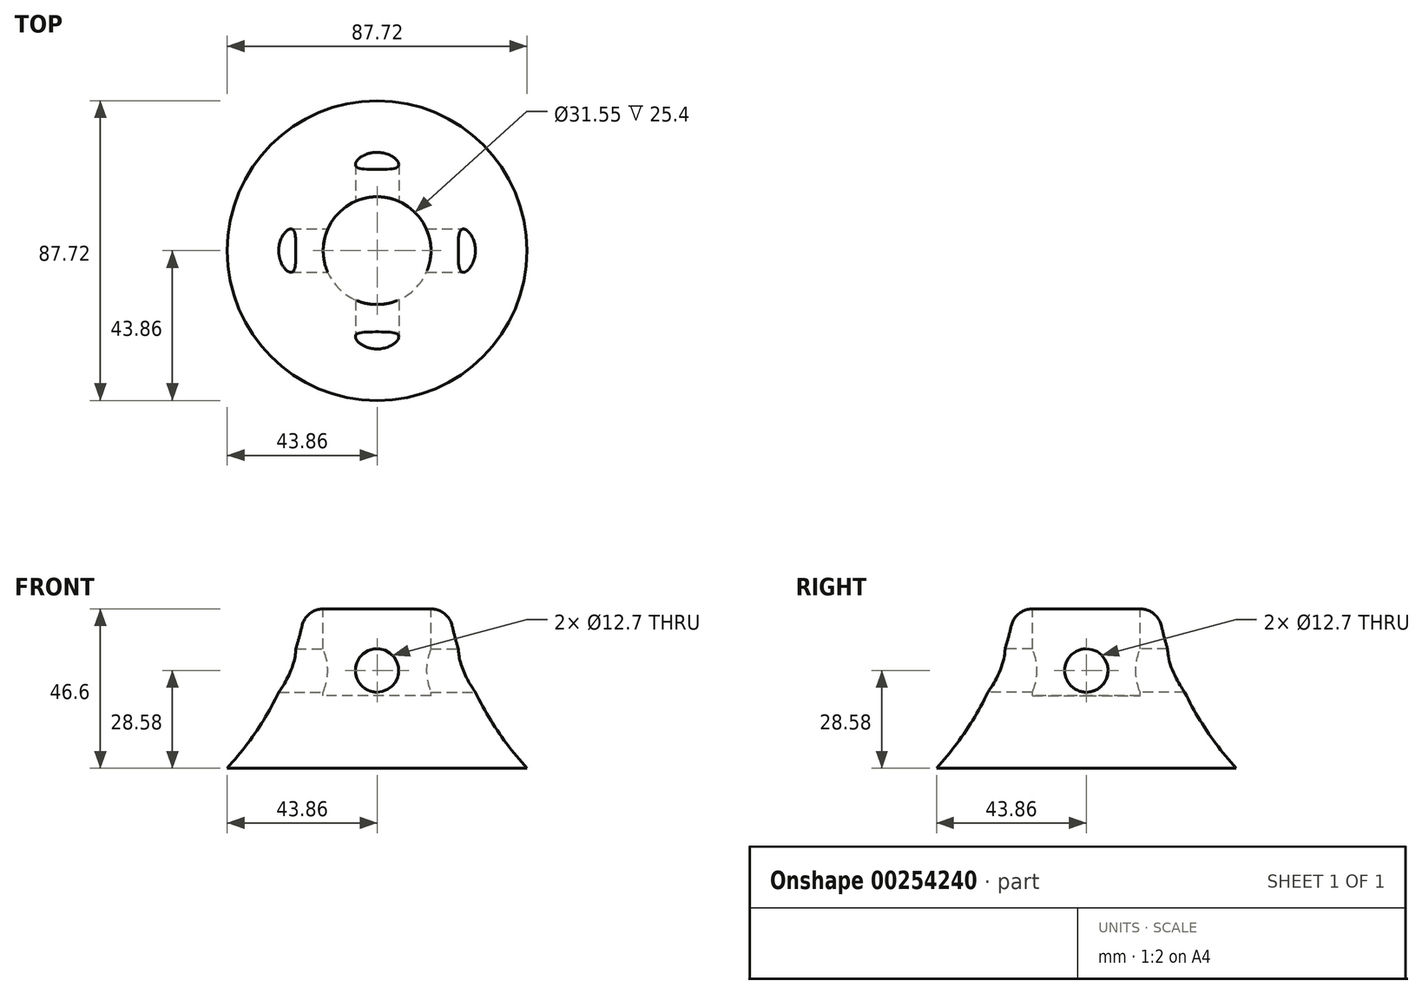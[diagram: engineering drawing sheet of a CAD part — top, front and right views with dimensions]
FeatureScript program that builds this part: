
annotation { "Feature Type Name" : "Feature", "Feature Type Description" : "" }
export const myFeature = defineFeature(function(context is Context, id is Id, definition is map)
    precondition{}
    {
        {
            var Q0;
            Q0=qCreatedBy(makeId("Front.planeOp"),FACE);
            var sketch = newSketch(context, id + "F0", { "sketchPlane" : qUnion([Q0])});
            skLineSegment(sketch, "E0", {"start": v(0, 0) * mm, "end": v(0, 49.77) * mm});
            skLineSegment(sketch, "E1", {"start": v(0, 49.77) * mm, "end": v(-15.76, 49.77) * mm});
            skLineSegment(sketch, "E2", {"start": v(0, 0) * mm, "end": v(-46.92, 0) * mm});
            skArc(sketch, "E3", {"start": v(-46.92, 0) * mm, "mid": v(-31.25, 20.64) * mm, "end": v(-21.95, 44.84) * mm});
            skPoint(sketch, "E4.visualSharp", {"position": v(-20.97, 49.77) * mm});
            skArc(sketch, "E4.filletArc", {"start": v(-15.76, 49.77) * mm, "mid": v(-19.72, 48.4) * mm, "end": v(-21.95, 44.84) * mm});
            skSolve(sketch);
        }
        {
            var Q0;
            Q0=makeQuery(id+"F0.imprint","IMPRINT",FACE,{"disambiguationData":[TD([[makeQuery(id+"F0.imprint","IMPRINT",EDGE,{"derivedFrom":sQuery(id+"F0.wireOp",EDGE,"E0")}),1.0]])]});
            var Q1;
            Q1=sQuery(id+"F0.wireOp",EDGE,"E0");
            revolve(context, id + "F1", {"entities" : qUnion([Q0]), "axis" : qUnion([Q1]), "revolveType" : RevolveType.FULL});
        }
        {
            var Q0;
            Q0=makeQuery(id+"F1.opRevolve","SWEPT_FACE",FACE,{"disambiguationData":[OSD([sQuery(id+"F0.wireOp",EDGE,"E1")])]});
            var sketch = newSketch(context, id + "F2", { "sketchPlane" : qUnion([Q0])});
            skCircle(sketch, "E5", {"center": v(0, 0) * mm, "radius": 15.77 * mm});
            skSolve(sketch);
        }
        {
            var Q0;
            Q0 = qSketchRegion(id + "F2", true);
            extrude(context, id + "F3", {"entities" : qUnion([Q0]), "operationType" : NewBodyOperationType.REMOVE, "oppositeDirection" : true, "depth" : 25.4 * mm});
        }
        {
            var Q0;
            Q0=makeQuery(id+"F1.opRevolve","SWEPT_FACE",FACE,{"disambiguationData":[OSD([sQuery(id+"F0.wireOp",EDGE,"E2")])]});
            var sketch = newSketch(context, id + "F4", { "sketchPlane" : qUnion([Q0])});
            skCircle(sketch, "E6", {"center": v(0, 0) * mm, "radius": 46.92 * mm});
            skSolve(sketch);
        }
        {
            var Q0;
            Q0=makeQuery(id+"F4.imprint","IMPRINT",FACE,{"disambiguationData":[TD([[makeQuery(id+"F4.imprint","IMPRINT",EDGE,{"derivedFrom":sQuery(id+"F4.wireOp",EDGE,"E6")}),1.0]])]});
            extrude(context, id + "F5", {"entities" : qUnion([Q0]), "operationType" : NewBodyOperationType.REMOVE, "oppositeDirection" : true, "depth" : 3.17 * mm});
        }
        {
            var Q0;
            Q0=qCreatedBy(makeId("Front.planeOp"),FACE);
            var sketch = newSketch(context, id + "F6", { "sketchPlane" : qUnion([Q0])});
            skCircle(sketch, "E7", {"center": v(0, 31.75) * mm, "radius": 6.35 * mm});
            skSolve(sketch);
        }
        {
            var Q0;
            Q0=makeQuery(id+"F6.imprint","IMPRINT",FACE,{"disambiguationData":[TD([[makeQuery(id+"F6.imprint","IMPRINT",EDGE,{"derivedFrom":sQuery(id+"F6.wireOp",EDGE,"E7")}),1.0]])]});
            extrude(context, id + "F7", {"entities" : qUnion([Q0]), "operationType" : NewBodyOperationType.REMOVE, "oppositeDirection" : true, "depth" : 79.25 * mm, "hasSecondDirection" : true, "secondDirectionOppositeDirection" : false, "secondDirectionDepth" : 87.63 * mm});
        }
        {
            var Q0;
            Q0=qCreatedBy(makeId("Right.planeOp"),FACE);
            var sketch = newSketch(context, id + "F8", { "sketchPlane" : qUnion([Q0])});
            skCircle(sketch, "E8", {"center": v(0, 31.75) * mm, "radius": 6.35 * mm});
            skSolve(sketch);
        }
        {
            var Q0;
            Q0=makeQuery(id+"F8.imprint","IMPRINT",FACE,{"disambiguationData":[TD([[makeQuery(id+"F8.imprint","IMPRINT",EDGE,{"derivedFrom":sQuery(id+"F8.wireOp",EDGE,"E8")}),1.0]])]});
            extrude(context, id + "F9", {"entities" : qUnion([Q0]), "operationType" : NewBodyOperationType.REMOVE, "oppositeDirection" : true, "depth" : 50.8 * mm, "hasSecondDirection" : true, "secondDirectionOppositeDirection" : false, "secondDirectionDepth" : 121.4 * mm});
        }
    });
